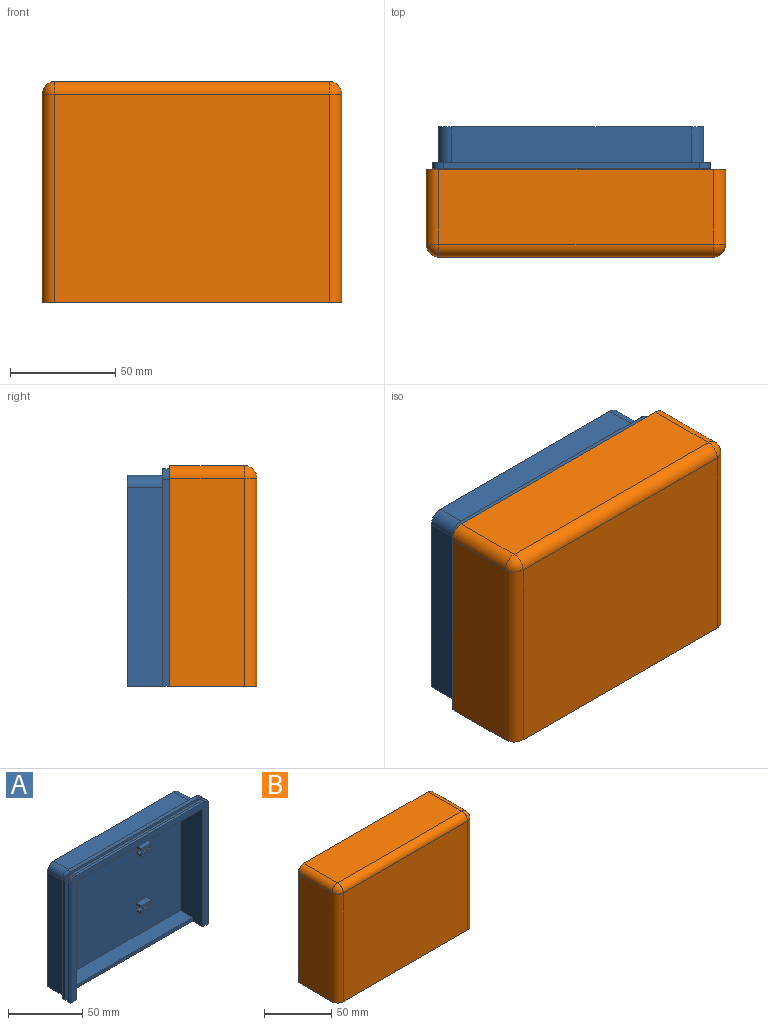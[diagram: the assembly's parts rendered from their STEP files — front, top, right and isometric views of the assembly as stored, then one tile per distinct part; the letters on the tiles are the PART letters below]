
ASSEMBLY  parts=2 mates=1
PART A: 70 faces, bbox 132.9x25x103.9 mm
  f0: plane 130.11x102.48mm, normal (0,-1,0), area 1618.3mm2, adj f3,f15,f32,f33,f34,f42,f43,f66
  f1: plane 132.11x103.48mm, normal (0,1,0), area 988.4mm2, adj f10,f11,f12,f15,f35,f36,f40,f42
  f2: plane 132.11x103.48mm, normal (0,1,0), area 1003.9mm2, adj f9,f14,f15,f16,f37,f39,f41,f44
  f3: cylinder r=1mm len=98.45mm, axis (0,0,1), area 154.6mm2, adj f0,f15,f36,f66
  f4: plane 10x2.25mm, normal (0,-1,0), area 22.5mm2, adj f5,f25,f26,f53
  f5: plane 7x5mm, normal (1,0,0), area 19.9mm2, adj f4,f13,f25,f27,f28,f53,f54,f55
  f6: plane 10x2.25mm, normal (0,-1,0), area 22.5mm2, adj f7,f8,f29,f52
  f7: plane 7x5mm, normal (1,0,0), area 19.9mm2, adj f6,f13,f29,f30,f31,f46,f47,f48
  f8: plane 7x5mm, normal (-1,0,0), area 19.9mm2, adj f6,f13,f29,f30,f31,f46,f47,f48
  f9: plane 94.45x17mm, normal (1,0,0), area 1605.6mm2, adj f2,f15,f17,f60
  f10: plane 100.45x2mm, normal (1,0,0), area 200.9mm2, adj f1,f11,f15,f38
  f11: plane 126.11x2mm, normal (0,0,1), area 252.2mm2, adj f1,f10,f12,f38
  f12: plane 100.45x2mm, normal (-1,0,0), area 200.9mm2, adj f1,f11,f15,f38
  f13: plane 114.11x94.45mm, normal (0,-1,0), area 10637.7mm2, adj f5,f7,f8,f18,f21,f25,f26,f27
  f14: plane 94.45x17mm, normal (-1,0,0), area 1605.6mm2, adj f2,f15,f17,f61
  f15: plane 129.11x25mm, normal (0,0,-1), area 2029.5mm2, adj f0,f1,f2,f3,f9,f10,f12,f14
  f16: plane 114.11x17mm, normal (0,0,1), area 1939.9mm2, adj f2,f17,f60,f61
  f17: plane 126.11x100.45mm, normal (0,1,0), area 12652.3mm2, adj f9,f14,f15,f16,f60,f61
  f18: plane 94.45x5.5mm, normal (1,0,0), area 519.5mm2, adj f13,f19,f21,f32
  f19: plane 94.45x3mm, normal (0,-1,0), area 283.3mm2, adj f18,f20,f21,f32
  f20: plane 94.45x3.25mm, normal (1,0,0), area 307mm2, adj f19,f21,f23,f32
  f21: plane 117.11x12mm, normal (0,0,1), area 1375.9mm2, adj f13,f18,f19,f20,f22,f23,f24,f34
  f22: plane 120.11x97.45mm, normal (0,-1,0), area 1021.5mm2, adj f15,f21,f24,f32,f33,f34
  f23: plane 94.45x4mm, normal (0,1,0), area 377.8mm2, adj f20,f21,f24,f32
  f24: plane 94.45x3.25mm, normal (1,0,0), area 307mm2, adj f21,f22,f23,f32
  f25: plane 10x5mm, normal (0,0,1), area 50mm2, adj f4,f5,f13,f26
  f26: plane 7x5mm, normal (-1,0,0), area 19.9mm2, adj f4,f13,f25,f27,f28,f53,f54,f55
  f27: plane 10x5mm, normal (0,0,-1), area 50mm2, adj f5,f13,f26,f28
  f28: plane 10x2.25mm, normal (0,-1,0), area 22.5mm2, adj f5,f26,f27,f54
  f29: plane 10x5mm, normal (0,0,1), area 50mm2, adj f6,f7,f8,f13
  f30: plane 10x5mm, normal (0,0,-1), area 50mm2, adj f7,f8,f13,f31
  f31: plane 10x2.25mm, normal (0,-1,0), area 22.5mm2, adj f7,f8,f30,f46
  f32: plane 120.11x21.5mm, normal (0,0,-1), area 2516.9mm2, adj f0,f13,f18,f19,f20,f22,f23,f24
  f33: plane 97.45x9.5mm, normal (1,0,0), area 925.8mm2, adj f0,f15,f22,f32
  f34: plane 97.45x21.5mm, normal (-1,0,0), area 2059.1mm2, adj f0,f13,f15,f21,f22,f32
  f35: plane 122.11x2mm, normal (0,0,1), area 244.2mm2, adj f1,f63,f64,f67
  f36: plane 98.45x2mm, normal (-1,0,0), area 196.9mm2, adj f1,f3,f15,f64
  f37: plane 122.11x3mm, normal (0,0,1), area 366.3mm2, adj f2,f38,f62,f65
  f38: plane 132.11x103.48mm, normal (0,-1,0), area 988.4mm2, adj f10,f11,f12,f15,f37,f39,f41,f44
  f39: plane 98.45x3mm, normal (-1,0,0), area 295.3mm2, adj f2,f15,f38,f65
  f40: plane 98.48x2mm, normal (1,0,0), area 197mm2, adj f1,f43,f63,f69
  f41: plane 98.48x3mm, normal (1,0,0), area 295.4mm2, adj f2,f38,f45,f62
  f42: plane 3x0.03mm, normal (-1,0,0), area 0.1mm2, adj f0,f1,f15,f43
  f43: plane 3x3mm, normal (0,0,-1), area 8.8mm2, adj f0,f1,f40,f42,f69
  f44: plane 3x0.03mm, normal (-1,0,0), area 0.1mm2, adj f2,f15,f38,f45
  f45: plane 3x3mm, normal (0,0,-1), area 9mm2, adj f2,f38,f41,f44
  f46: plane 10x1.2mm, normal (0,0,1), area 12mm2, adj f7,f8,f31,f47
  f47: plane 10x0.55mm, normal (0,0.67,0.74), area 7.4mm2, adj f7,f8,f46,f48
  f48: plane 10x3mm, normal (0,0,1), area 30mm2, adj f7,f8,f47,f49
  f49: plane 10x3.5mm, normal (0,-1,0), area 35mm2, adj f7,f8,f48,f50
  f50: plane 10x3mm, normal (0,0,-1), area 30mm2, adj f7,f8,f49,f51
  f51: plane 10x0.55mm, normal (0,0.67,-0.74), area 7.4mm2, adj f7,f8,f50,f52
  f52: plane 10x1.2mm, normal (0,0,-1), area 12mm2, adj f6,f7,f8,f51
  f53: plane 10x1.2mm, normal (0,0,-1), area 12mm2, adj f4,f5,f26,f59
  f54: plane 10x1.2mm, normal (0,0,1), area 12mm2, adj f5,f26,f28,f55
  f55: plane 10x0.55mm, normal (0,0.67,0.74), area 7.4mm2, adj f5,f26,f54,f56
  f56: plane 10x3mm, normal (0,0,1), area 30mm2, adj f5,f26,f55,f57
  f57: plane 10x3.5mm, normal (0,-1,0), area 35mm2, adj f5,f26,f56,f58
  f58: plane 10x3mm, normal (0,0,-1), area 30mm2, adj f5,f26,f57,f59
  f59: plane 10x0.55mm, normal (0,0.67,-0.74), area 7.4mm2, adj f5,f26,f53,f58
  f60: cylinder r=6mm len=17mm, axis (0,-1,0), area 160.2mm2, adj f2,f9,f16,f17
  f61: cylinder r=6mm len=17mm, axis (0,1,0), area 160.2mm2, adj f2,f14,f16,f17
  f62: cylinder r=5mm len=5mm, axis (0,1,0), area 23.6mm2, adj f2,f37,f38,f41
  f63: cylinder r=5mm len=5mm, axis (0,1,0), area 15.7mm2, adj f1,f35,f40,f68
  f64: cylinder r=5mm len=5mm, axis (0,-1,0), area 15.7mm2, adj f1,f35,f36,f66
  f65: cylinder r=5mm len=5mm, axis (0,-1,0), area 23.6mm2, adj f2,f37,f38,f39
  f66: torus R=4mm, axis (0,-1,0), area 11.4mm2, adj f0,f3,f64,f67
  f67: cylinder r=1mm len=122.11mm, axis (1,0,0), area 191.8mm2, adj f0,f35,f66,f68
  f68: torus R=4mm, axis (0,-1,0), area 11.4mm2, adj f0,f63,f67,f69
  f69: cylinder r=1mm len=98.48mm, axis (0,0,-1), area 154.7mm2, adj f0,f40,f43,f68
PART B: 28 faces, bbox 142.5x41.5x105 mm
  f0: plane 142.5x41.5mm, normal (0,0,-1), area 557.6mm2, adj f1,f2,f4,f5,f6,f9,f13,f15
  f1: plane 137.5x102.5mm, normal (0,-1,0), area 1471mm2, adj f0,f13,f14,f15,f18,f23,f25,f26
  f2: plane 99x35.5mm, normal (1,0,0), area 3514.5mm2, adj f0,f9,f12,f24
  f3: plane 130.5x35.5mm, normal (0,0,1), area 4632.8mm2, adj f7,f10,f12,f24
  f4: plane 99x35.5mm, normal (-1,0,0), area 3514.5mm2, adj f0,f6,f7,f24
  f5: plane 130.5x99mm, normal (0,-1,0), area 12919.5mm2, adj f0,f6,f9,f10
  f6: cylinder r=6mm len=99mm, axis (0,0,1), area 933.1mm2, adj f0,f4,f5,f8
  f7: cylinder r=6mm len=35.5mm, axis (0,1,0), area 334.6mm2, adj f3,f4,f8,f24
  f8: sphere r=6mm, area 56.5mm2, adj f6,f7,f10
  f9: cylinder r=6mm len=99mm, axis (0,0,-1), area 933.1mm2, adj f0,f2,f5,f11
  f10: cylinder r=6mm len=130.5mm, axis (1,0,0), area 1229.9mm2, adj f3,f5,f8,f11
  f11: sphere r=6mm, area 56.5mm2, adj f9,f10,f12
  f12: cylinder r=6mm len=35.5mm, axis (0,-1,0), area 334.6mm2, adj f2,f3,f11,f24
  f13: plane 99x34mm, normal (-1,0,0), area 3366mm2, adj f0,f1,f20,f23
  f14: plane 130.5x34mm, normal (0,0,-1), area 4437mm2, adj f1,f18,f21,f23
  f15: plane 99x34mm, normal (1,0,0), area 3366mm2, adj f0,f1,f17,f18
  f16: plane 130.5x99mm, normal (0,1,0), area 12919.5mm2, adj f0,f17,f20,f21
  f17: cylinder r=3.5mm len=99mm, axis (0,0,1), area 544.3mm2, adj f0,f15,f16,f19
  f18: cylinder r=3.5mm len=34mm, axis (0,1,0), area 186.9mm2, adj f1,f14,f15,f19
  f19: sphere r=3.5mm, area 19.2mm2, adj f17,f18,f21
  f20: cylinder r=3.5mm len=99mm, axis (0,0,-1), area 544.3mm2, adj f0,f13,f16,f22
  f21: cylinder r=3.5mm len=130.5mm, axis (1,0,0), area 717.5mm2, adj f14,f16,f19,f22
  f22: sphere r=3.5mm, area 19.2mm2, adj f20,f21,f23
  f23: cylinder r=3.5mm len=34mm, axis (0,-1,0), area 186.9mm2, adj f1,f13,f14,f22
  f24: plane 142.5x105mm, normal (0,1,0), area 2329.6mm2, adj f0,f2,f3,f4,f7,f12,f25,f26
  f25: plane 126.49x1.5mm, normal (-0.01,0,-1), area 189.7mm2, adj f1,f24,f26,f27
  f26: plane 99x1.5mm, normal (-1,0,0), area 148.5mm2, adj f0,f1,f24,f25
  f27: plane 100.5x1.5mm, normal (1,0,0), area 150.7mm2, adj f0,f1,f24,f25
PLACE A t=(-52.06,-106.67,12.63)mm
PLACE B t=(-51.16,-128.42,15.13)mm
MATE parallel B.f27 <-> A.f12  axis (1,0,0) through (-116.41,-127.67,63.13)mm
